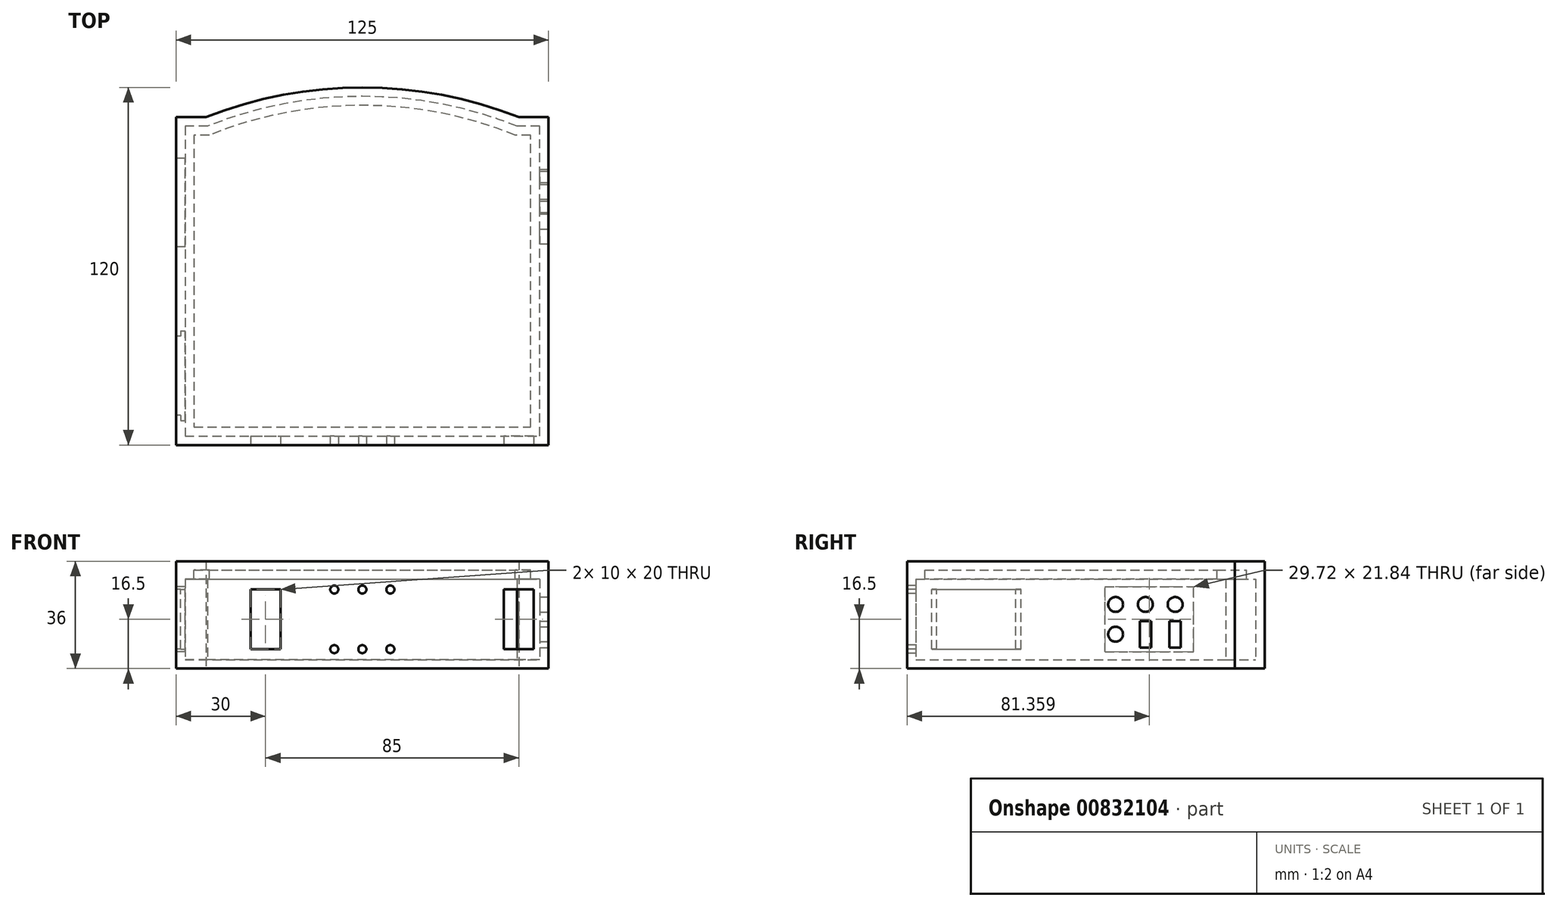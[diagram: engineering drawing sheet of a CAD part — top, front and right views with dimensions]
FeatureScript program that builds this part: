
annotation { "Feature Type Name" : "Feature", "Feature Type Description" : "" }
export const myFeature = defineFeature(function(context is Context, id is Id, definition is map)
    precondition{}
    {
        {
            var Q0;
            Q0=qCreatedBy(makeId("Top.planeOp"),FACE);
            var sketch = newSketch(context, id + "F0", { "sketchPlane" : qUnion([Q0])});
            skLineSegment(sketch, "E0", {"start": v(0, 0) * mm, "end": v(125, 0) * mm});
            skLineSegment(sketch, "E1", {"start": v(125, 0) * mm, "end": v(125, 110) * mm});
            skLineSegment(sketch, "E2", {"start": v(0, 0) * mm, "end": v(0, 110) * mm});
            skLineSegment(sketch, "E3", {"start": v(0, 110) * mm, "end": v(10, 110) * mm});
            skLineSegment(sketch, "E4", {"start": v(125, 110) * mm, "end": v(115, 110) * mm});
            skArc(sketch, "E5", {"start": v(115, 110) * mm, "mid": v(62.5, 120) * mm, "end": v(10, 110) * mm});
            skSolve(sketch);
        }
        {
            var Q0;
            Q0=makeQuery(id+"F0.imprint","IMPRINT",FACE,{"disambiguationData":[TD([[makeQuery(id+"F0.imprint","IMPRINT",EDGE,{"derivedFrom":sQuery(id+"F0.wireOp",EDGE,"E0")}),1.0]])]});
            extrude(context, id + "F1", {"entities" : qUnion([Q0]), "depth" : 3 * mm, "offsetDistance" : 25 * mm});
        }
        {
            var Q0;
            Q0=makeQuery(id+"F1.opExtrude","CAP_FACE",FACE,{"disambiguationData":[OSD([sQuery(id+"F0.wireOp",EDGE,"E0"),sQuery(id+"F0.wireOp",EDGE,"E1"),sQuery(id+"F0.wireOp",EDGE,"E2"),sQuery(id+"F0.wireOp",EDGE,"E3"),sQuery(id+"F0.wireOp",EDGE,"E4"),sQuery(id+"F0.wireOp",EDGE,"E5")])],"isStart":false});
            var sketch = newSketch(context, id + "F2", { "sketchPlane" : qUnion([Q0])});
            skLineSegment(sketch, "E6.0", {"start": v(122, 3) * mm, "end": v(122, 107) * mm});
            skArc(sketch, "E6.1", {"start": v(114.43, 107) * mm, "mid": v(62.5, 117) * mm, "end": v(10.57, 107) * mm});
            skLineSegment(sketch, "E6.2", {"start": v(10.57, 107) * mm, "end": v(3, 107) * mm});
            skLineSegment(sketch, "E6.3", {"start": v(122, 107) * mm, "end": v(114.43, 107) * mm});
            skLineSegment(sketch, "E6.4", {"start": v(3, 107) * mm, "end": v(3, 3) * mm});
            skLineSegment(sketch, "E6.5", {"start": v(3, 3) * mm, "end": v(122, 3) * mm});
            skSolve(sketch);
        }
        {
            var Q0;
            Q0=makeQuery(id+"F2.imprint","IMPRINT",FACE,{"disambiguationData":[TD([[makeQuery(id+"F2.imprint","IMPRINT",EDGE,{"derivedFrom":sQuery(id+"F2.wireOp",EDGE,"E6.0")}),-1.0]])]});
            extrude(context, id + "F3", {"entities" : qUnion([Q0]), "operationType" : NewBodyOperationType.ADD, "depth" : 30 * mm, "offsetDistance" : 25 * mm});
        }
        {
            var Q0;
            {var subQ0=sQuery(id+"F0.wireOp",EDGE,"E2");Q0=makeQuery(id+"F3.boolean.opBoolean","MERGE",FACE,{"derivedFrom":[makeQuery(id+"F1.opExtrude","SWEPT_FACE",FACE,{"disambiguationData":[OSD([subQ0])]}),makeQuery(id+"F3.opExtrude","SWEPT_FACE",FACE,{"disambiguationData":[OSD([subQ0])]})]});}
            var sketch = newSketch(context, id + "F4", { "sketchPlane" : qUnion([Q0])});
            skLineSegment(sketch, "E7.bottom", {"start": v(-10, 6.5) * mm, "end": v(-36.5, 6.5) * mm});
            skLineSegment(sketch, "E7.top", {"start": v(-10, 26.5) * mm, "end": v(-36.5, 26.5) * mm});
            skLineSegment(sketch, "E7.left", {"start": v(-10, 6.5) * mm, "end": v(-10, 26.5) * mm});
            skLineSegment(sketch, "E7.right", {"start": v(-36.5, 6.5) * mm, "end": v(-36.5, 26.5) * mm});
            skPoint(sketch, "E8", {"position": v(-10, 16.5) * mm});
            skPoint(sketch, "E9", {"position": v(0, 16.5) * mm});
            skSolve(sketch);
        }
        {
            var Q0;
            Q0=makeQuery(id+"F4.imprint","IMPRINT",FACE,{"disambiguationData":[TD([[makeQuery(id+"F4.imprint","IMPRINT",EDGE,{"derivedFrom":sQuery(id+"F4.wireOp",EDGE,"E7.bottom")}),-1.0]])]});
            extrude(context, id + "F5", {"entities" : qUnion([Q0]), "operationType" : NewBodyOperationType.REMOVE, "endBound" : BoundingType.UP_TO_NEXT, "oppositeDirection" : true, "depth" : 25 * mm, "offsetDistance" : 25 * mm});
        }
        {
            var Q0;
            Q0=makeQuery(id+"F3.opExtrude","SWEPT_FACE",FACE,{"disambiguationData":[OSD([sQuery(id+"F2.wireOp",EDGE,"E6.4")])]});
            var sketch = newSketch(context, id + "F6", { "sketchPlane" : qUnion([Q0])});
            skLineSegment(sketch, "E10.bottom", {"start": v(38.25, 6.5) * mm, "end": v(8.25, 6.5) * mm});
            skLineSegment(sketch, "E10.top", {"start": v(38.25, 26.5) * mm, "end": v(8.25, 26.5) * mm});
            skLineSegment(sketch, "E10.left", {"start": v(38.25, 6.5) * mm, "end": v(38.25, 26.5) * mm});
            skLineSegment(sketch, "E10.right", {"start": v(8.25, 6.5) * mm, "end": v(8.25, 26.5) * mm});
            skPoint(sketch, "E11", {"position": v(23.25, 6.5) * mm});
            skSolve(sketch);
        }
        {
            var Q0;
            Q0 = qSketchRegion(id + "F6", true);
            extrude(context, id + "F7", {"entities" : qUnion([Q0]), "operationType" : NewBodyOperationType.REMOVE, "oppositeDirection" : true, "depth" : 1.5 * mm, "offsetDistance" : 25 * mm});
        }
        {
            var Q0;
            {var subQ0=sQuery(id+"F0.wireOp",EDGE,"E2");Q0=makeQuery(id+"F3.boolean.opBoolean","MERGE",FACE,{"derivedFrom":[makeQuery(id+"F1.opExtrude","SWEPT_FACE",FACE,{"disambiguationData":[OSD([subQ0])]}),makeQuery(id+"F3.opExtrude","SWEPT_FACE",FACE,{"disambiguationData":[OSD([subQ0])]})]});}
            var sketch = newSketch(context, id + "F8", { "sketchPlane" : qUnion([Q0])});
            skLineSegment(sketch, "E12.bottom", {"start": v(-66.5, 5.58) * mm, "end": v(-96.22, 5.58) * mm});
            skLineSegment(sketch, "E12.top", {"start": v(-66.5, 27.42) * mm, "end": v(-96.22, 27.42) * mm});
            skLineSegment(sketch, "E12.left", {"start": v(-66.5, 5.58) * mm, "end": v(-66.5, 27.42) * mm});
            skLineSegment(sketch, "E12.right", {"start": v(-96.22, 5.58) * mm, "end": v(-96.22, 27.42) * mm});
            skPoint(sketch, "E13", {"position": v(-66.5, 16.5) * mm});
            skPoint(sketch, "E14", {"position": v(0, 16.5) * mm});
            skSolve(sketch);
        }
        {
            var Q0;
            Q0=makeQuery(id+"F8.imprint","IMPRINT",FACE,{"disambiguationData":[TD([[makeQuery(id+"F8.imprint","IMPRINT",EDGE,{"derivedFrom":sQuery(id+"F8.wireOp",EDGE,"E12.bottom")}),-1.0]])]});
            extrude(context, id + "F9", {"entities" : qUnion([Q0]), "operationType" : NewBodyOperationType.REMOVE, "endBound" : BoundingType.UP_TO_NEXT, "oppositeDirection" : true, "depth" : 25 * mm, "offsetDistance" : 25 * mm});
        }
        {
            var Q0;
            {var subQ0=sQuery(id+"F0.wireOp",EDGE,"E0");Q0=makeQuery(id+"F3.boolean.opBoolean","MERGE",FACE,{"derivedFrom":[makeQuery(id+"F1.opExtrude","SWEPT_FACE",FACE,{"disambiguationData":[OSD([subQ0])]}),makeQuery(id+"F3.opExtrude","SWEPT_FACE",FACE,{"disambiguationData":[OSD([subQ0])]})]});}
            var sketch = newSketch(context, id + "F10", { "sketchPlane" : qUnion([Q0])});
            skLineSegment(sketch, "E15.bottom", {"start": v(25, 26.5) * mm, "end": v(35, 26.5) * mm});
            skLineSegment(sketch, "E15.top", {"start": v(25, 6.5) * mm, "end": v(35, 6.5) * mm});
            skLineSegment(sketch, "E15.left", {"start": v(25, 26.5) * mm, "end": v(25, 6.5) * mm});
            skLineSegment(sketch, "E15.right", {"start": v(35, 26.5) * mm, "end": v(35, 6.5) * mm});
            skPoint(sketch, "E15.middle", {"position": v(30, 16.5) * mm});
            skPoint(sketch, "E15.middle.positionSnap0", {"position": v(0, 16.5) * mm});
            skPoint(sketch, "E15.centerSnap0", {"position": v(0, 16.5) * mm});
            skLineSegment(sketch, "E16.bottom", {"start": v(120, 26.5) * mm, "end": v(110, 26.5) * mm});
            skLineSegment(sketch, "E16.top", {"start": v(120, 6.5) * mm, "end": v(110, 6.5) * mm});
            skLineSegment(sketch, "E16.left", {"start": v(120, 26.5) * mm, "end": v(120, 6.5) * mm});
            skLineSegment(sketch, "E16.right", {"start": v(110, 26.5) * mm, "end": v(110, 6.5) * mm});
            skPoint(sketch, "E16.middle", {"position": v(115, 16.5) * mm});
            skPoint(sketch, "E16.middle.positionSnap0", {"position": v(125, 16.5) * mm});
            skPoint(sketch, "E16.centerSnap0", {"position": v(125, 16.5) * mm});
            skSolve(sketch);
        }
        {
            var Q0;
            Q0=makeQuery(id+"F10.imprint","IMPRINT",FACE,{"disambiguationData":[TD([[makeQuery(id+"F10.imprint","IMPRINT",EDGE,{"derivedFrom":sQuery(id+"F10.wireOp",EDGE,"E15.bottom")}),-1.0]])]});
            var Q1;
            Q1=makeQuery(id+"F10.imprint","IMPRINT",FACE,{"disambiguationData":[TD([[makeQuery(id+"F10.imprint","IMPRINT",EDGE,{"derivedFrom":sQuery(id+"F10.wireOp",EDGE,"E16.bottom")}),1.0]])]});
            extrude(context, id + "F11", {"entities" : qUnion([Q0, Q1]), "operationType" : NewBodyOperationType.REMOVE, "endBound" : BoundingType.UP_TO_NEXT, "oppositeDirection" : true, "depth" : 25 * mm, "offsetDistance" : 25 * mm});
        }
        {
            var Q0;
            {var subQ0=sQuery(id+"F0.wireOp",EDGE,"E1");Q0=makeQuery(id+"F3.boolean.opBoolean","MERGE",FACE,{"derivedFrom":[makeQuery(id+"F1.opExtrude","SWEPT_FACE",FACE,{"disambiguationData":[OSD([subQ0])]}),makeQuery(id+"F3.opExtrude","SWEPT_FACE",FACE,{"disambiguationData":[OSD([subQ0])]})]});}
            var sketch = newSketch(context, id + "F12", { "sketchPlane" : qUnion([Q0])});
            skCircle(sketch, "E17", {"center": v(90, 21.5) * mm, "radius": 2.5 * mm});
            skCircle(sketch, "E18", {"center": v(80, 21.5) * mm, "radius": 2.5 * mm});
            skCircle(sketch, "E19", {"center": v(70, 21.5) * mm, "radius": 2.5 * mm});
            skCircle(sketch, "E20", {"center": v(70, 11.5) * mm, "radius": 2.5 * mm});
            skLineSegment(sketch, "E21.bottom", {"start": v(78.1, 15.94) * mm, "end": v(81.9, 15.94) * mm});
            skLineSegment(sketch, "E21.top", {"start": v(78.1, 7.06) * mm, "end": v(81.9, 7.06) * mm});
            skLineSegment(sketch, "E21.left", {"start": v(78.1, 15.94) * mm, "end": v(78.1, 7.05) * mm});
            skLineSegment(sketch, "E21.right", {"start": v(81.9, 15.94) * mm, "end": v(81.9, 7.05) * mm});
            skPoint(sketch, "E21.middle", {"position": v(80, 11.5) * mm});
            skLineSegment(sketch, "E22.bottom", {"start": v(88.1, 15.94) * mm, "end": v(91.9, 15.94) * mm});
            skLineSegment(sketch, "E22.top", {"start": v(88.1, 7.05) * mm, "end": v(91.9, 7.05) * mm});
            skLineSegment(sketch, "E22.left", {"start": v(88.1, 15.94) * mm, "end": v(88.1, 7.05) * mm});
            skLineSegment(sketch, "E22.right", {"start": v(91.9, 15.95) * mm, "end": v(91.9, 7.05) * mm});
            skPoint(sketch, "E22.middle", {"position": v(90, 11.5) * mm});
            skLineSegment(sketch, "E23", {"start": v(90, 21.5) * mm, "end": v(90, 11.5) * mm, "construction": true});
            skPoint(sketch, "E24", {"position": v(90, 16.5) * mm});
            skPoint(sketch, "E25", {"position": v(110, 16.5) * mm});
            skSolve(sketch);
        }
        {
            var Q0;
            Q0 = qSketchRegion(id + "F12", true);
            extrude(context, id + "F13", {"entities" : qUnion([Q0]), "operationType" : NewBodyOperationType.REMOVE, "endBound" : BoundingType.UP_TO_NEXT, "oppositeDirection" : true, "depth" : 25 * mm, "offsetDistance" : 25 * mm});
        }
        {
            var Q0;
            Q0=makeQuery(id+"F3.opExtrude","CAP_FACE",FACE,{"disambiguationData":[OSD([sQuery(id+"F0.wireOp",EDGE,"E0"),sQuery(id+"F0.wireOp",EDGE,"E1"),sQuery(id+"F0.wireOp",EDGE,"E2"),sQuery(id+"F0.wireOp",EDGE,"E3"),sQuery(id+"F0.wireOp",EDGE,"E4"),sQuery(id+"F0.wireOp",EDGE,"E5"),sQuery(id+"F2.wireOp",EDGE,"E6.0"),sQuery(id+"F2.wireOp",EDGE,"E6.1"),sQuery(id+"F2.wireOp",EDGE,"E6.2"),sQuery(id+"F2.wireOp",EDGE,"E6.3"),sQuery(id+"F2.wireOp",EDGE,"E6.4"),sQuery(id+"F2.wireOp",EDGE,"E6.5")])],"isStart":false});
            var sketch = newSketch(context, id + "F14", { "sketchPlane" : qUnion([Q0])});
            skLineSegment(sketch, "E26.0", {"start": v(0, 0) * mm, "end": v(125, 0) * mm});
            skLineSegment(sketch, "E27.0", {"start": v(0, 0) * mm, "end": v(0, 110) * mm});
            skLineSegment(sketch, "E28.0", {"start": v(0, 110) * mm, "end": v(10, 110) * mm});
            skArc(sketch, "E29.0", {"start": v(115, 110) * mm, "mid": v(62.5, 120) * mm, "end": v(10, 110) * mm});
            skLineSegment(sketch, "E30.0", {"start": v(125, 110) * mm, "end": v(115, 110) * mm});
            skLineSegment(sketch, "E31.0", {"start": v(125, 0) * mm, "end": v(125, 110) * mm});
            skSolve(sketch);
        }
        {
            var Q0;
            Q0 = qSketchRegion(id + "F14", true);
            extrude(context, id + "F15", {"entities" : qUnion([Q0]), "depth" : 3 * mm, "offsetDistance" : 25 * mm});
        }
        {
            var Q0;
            Q0=makeQuery(id+"F15.opExtrude","CAP_FACE",FACE,{"disambiguationData":[OSD([sQuery(id+"F14.wireOp",EDGE,"E26.0"),sQuery(id+"F14.wireOp",EDGE,"E27.0"),sQuery(id+"F14.wireOp",EDGE,"E28.0"),sQuery(id+"F14.wireOp",EDGE,"E29.0"),sQuery(id+"F14.wireOp",EDGE,"E30.0"),sQuery(id+"F14.wireOp",EDGE,"E31.0")])],"isStart":true});
            var sketch = newSketch(context, id + "F16", { "sketchPlane" : qUnion([Q0])});
            skLineSegment(sketch, "E32.0", {"start": v(3, -107) * mm, "end": v(3, -3) * mm});
            skLineSegment(sketch, "E33.0", {"start": v(10.57, -107) * mm, "end": v(3, -107) * mm});
            skArc(sketch, "E34.0", {"start": v(114.43, -107) * mm, "mid": v(62.5, -117) * mm, "end": v(10.57, -107) * mm});
            skLineSegment(sketch, "E35.0", {"start": v(122, -107) * mm, "end": v(114.43, -107) * mm});
            skLineSegment(sketch, "E36.0", {"start": v(122, -3) * mm, "end": v(122, -107) * mm});
            skLineSegment(sketch, "E37.0", {"start": v(3, -3) * mm, "end": v(122, -3) * mm});
            skLineSegment(sketch, "E38.0", {"start": v(119, -104) * mm, "end": v(113.84, -104) * mm});
            skLineSegment(sketch, "E38.1", {"start": v(11.16, -104) * mm, "end": v(6, -104) * mm});
            skLineSegment(sketch, "E38.2", {"start": v(6, -104) * mm, "end": v(6, -6) * mm});
            skArc(sketch, "E38.3", {"start": v(113.84, -104) * mm, "mid": v(62.5, -114) * mm, "end": v(11.16, -104) * mm});
            skLineSegment(sketch, "E38.4", {"start": v(6, -6) * mm, "end": v(119, -6) * mm});
            skLineSegment(sketch, "E38.5", {"start": v(119, -6) * mm, "end": v(119, -104) * mm});
            skSolve(sketch);
        }
        {
            var Q0;
            Q0=makeQuery(id+"F16.imprint","IMPRINT",FACE,{"disambiguationData":[TD([[makeQuery(id+"F16.imprint","IMPRINT",EDGE,{"derivedFrom":sQuery(id+"F16.wireOp",EDGE,"E32.0")}),-1.0]])]});
            extrude(context, id + "F17", {"entities" : qUnion([Q0]), "operationType" : NewBodyOperationType.ADD, "depth" : 3 * mm, "offsetDistance" : 25 * mm});
        }
        {
            var Q0;
            {var subQ0=sQuery(id+"F0.wireOp",EDGE,"E0");Q0=makeQuery(id+"F3.boolean.opBoolean","MERGE",FACE,{"derivedFrom":[makeQuery(id+"F1.opExtrude","SWEPT_FACE",FACE,{"disambiguationData":[OSD([subQ0])]}),makeQuery(id+"F3.opExtrude","SWEPT_FACE",FACE,{"disambiguationData":[OSD([subQ0])]})]});}
            var sketch = newSketch(context, id + "F18", { "sketchPlane" : qUnion([Q0])});
            skPoint(sketch, "E39.0", {"position": v(62.5, 0) * mm});
            skPoint(sketch, "E40.0", {"position": v(0, 16.5) * mm});
            skCircle(sketch, "E41", {"center": v(53.09, 6.5) * mm, "radius": 1.35 * mm});
            skCircle(sketch, "E42.0.1.0", {"center": v(53.09, 26.5) * mm, "radius": 1.35 * mm});
            skCircle(sketch, "E42.1.0.0", {"center": v(62.5, 6.5) * mm, "radius": 1.35 * mm});
            skCircle(sketch, "E42.1.1.0", {"center": v(62.5, 26.5) * mm, "radius": 1.35 * mm});
            skCircle(sketch, "E42.2.0.0", {"center": v(71.91, 6.5) * mm, "radius": 1.35 * mm});
            skCircle(sketch, "E42.2.1.0", {"center": v(71.91, 26.5) * mm, "radius": 1.35 * mm});
            skLineSegment(sketch, "E42.direction1", {"start": v(53.09, 6.5) * mm, "end": v(62.5, 6.5) * mm, "construction": true});
            skLineSegment(sketch, "E42.direction2", {"start": v(53.09, 6.5) * mm, "end": v(53.09, 26.5) * mm, "construction": true});
            skPoint(sketch, "E43", {"position": v(53.09, 16.5) * mm});
            skSolve(sketch);
        }
        {
            var Q0;
            Q0 = qSketchRegion(id + "F18", true);
            extrude(context, id + "F19", {"entities" : qUnion([Q0]), "operationType" : NewBodyOperationType.REMOVE, "endBound" : BoundingType.UP_TO_NEXT, "oppositeDirection" : true, "depth" : 25 * mm, "offsetDistance" : 25 * mm});
        }
    });
